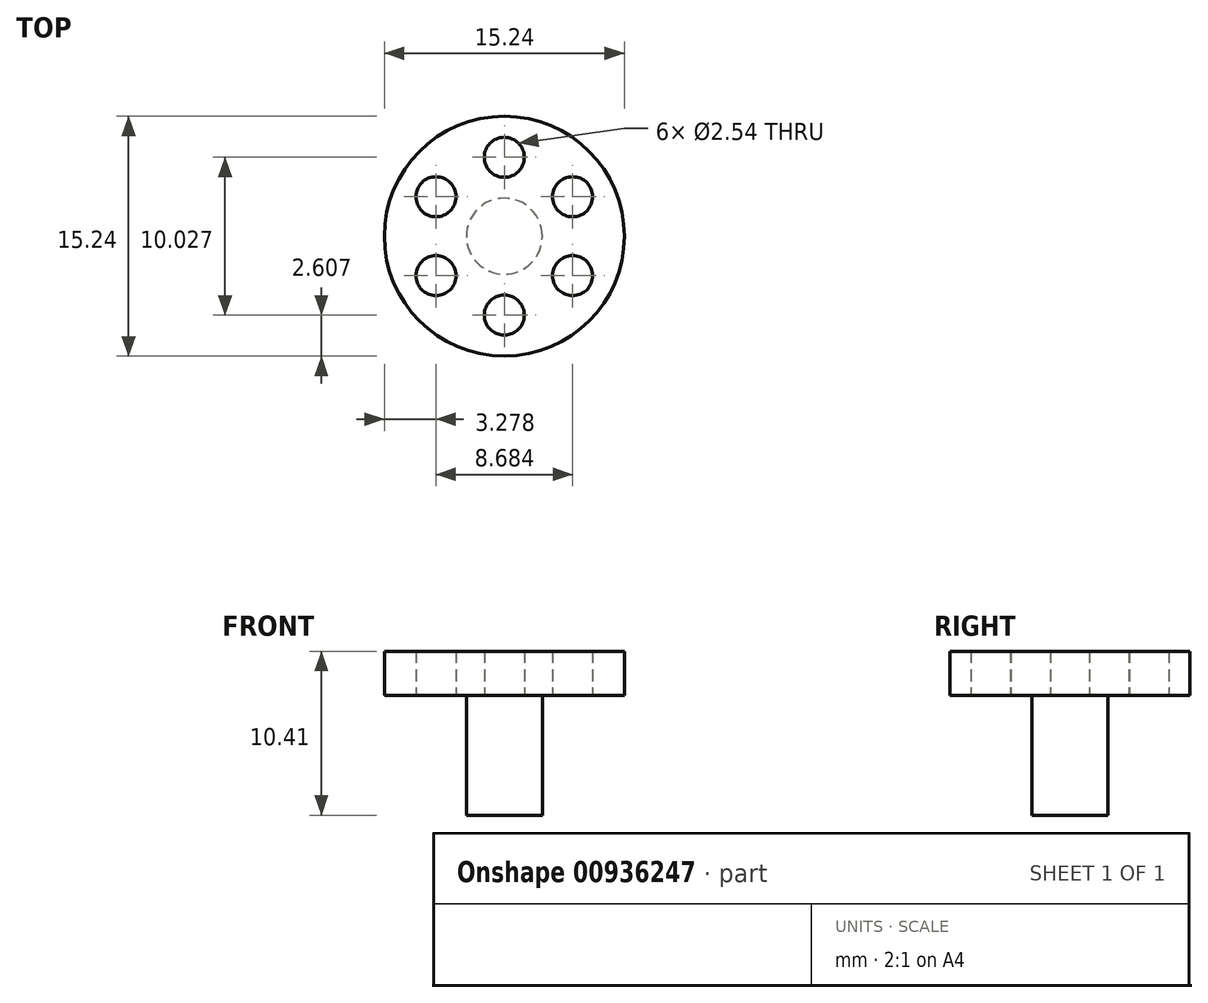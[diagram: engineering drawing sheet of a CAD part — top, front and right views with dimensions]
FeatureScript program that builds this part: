
annotation { "Feature Type Name" : "Feature", "Feature Type Description" : "" }
export const myFeature = defineFeature(function(context is Context, id is Id, definition is map)
    precondition{}
    {
        {
            var Q0;
            Q0=qCreatedBy(makeId("Top.planeOp"),FACE);
            var sketch = newSketch(context, id + "F0", { "sketchPlane" : qUnion([Q0])});
            skCircle(sketch, "E0", {"center": v(0, 0) * mm, "radius": 2.41 * mm});
            skSolve(sketch);
        }
        {
            var Q0;
            Q0 = qSketchRegion(id + "F0", true);
            extrude(context, id + "F1", {"entities" : qUnion([Q0]), "depth" : 7.62 * mm, "offsetDistance" : 25.4 * mm});
        }
        {
            var Q0;
            Q0=makeQuery(id+"F1.opExtrude","CAP_FACE",FACE,{"disambiguationData":[OSD([sQuery(id+"F0.wireOp",EDGE,"E0")])],"isStart":false});
            var sketch = newSketch(context, id + "F2", { "sketchPlane" : qUnion([Q0])});
            skCircle(sketch, "E1", {"center": v(0, 0) * mm, "radius": 7.62 * mm});
            skCircle(sketch, "E2", {"center": v(0, 5.01) * mm, "radius": 1.27 * mm});
            skCircle(sketch, "E3.1.0", {"center": v(-4.34, 2.5) * mm, "radius": 1.27 * mm});
            skCircle(sketch, "E3.2.0", {"center": v(-4.34, -2.5) * mm, "radius": 1.27 * mm});
            skCircle(sketch, "E3.3.0", {"center": v(0, -5.01) * mm, "radius": 1.27 * mm});
            skCircle(sketch, "E3.4.0", {"center": v(4.34, -2.5) * mm, "radius": 1.27 * mm});
            skCircle(sketch, "E3.5.0", {"center": v(4.34, 2.5) * mm, "radius": 1.27 * mm});
            skSolve(sketch);
        }
        {
            var Q0;
            Q0 = qSketchRegion(id + "F2", true);
            extrude(context, id + "F3", {"entities" : qUnion([Q0]), "operationType" : NewBodyOperationType.ADD, "depth" : 2.8 * mm, "offsetDistance" : 25.4 * mm});
        }
    });
